# Revit family: VT.VAR11.G.07
name_source: partatom
category: Оборудование
units: mm (PartAtom-declared; Revit-internal decimal feet)

## family parameters
Всегда вертикально = Да
Заголовок OmniClass = Climate Control (HVAC)
На основе рабочей плоскости = Нет
Номер OmniClass = 23.75.00.00
Общий = Нет
При загрузке вырезать с полостями = Нет
Размер круглого соединителя = Использовать диаметр
Тип детали = Нормальный
Точка расчета площади = Нет

## types (1)
- VT.VAR11.G.07
    BIMобъект категории = Другие
    BIMобъект основная категория = Водопровод
    Design country = Italy
    Edition number = 2
    Manifacturer URL = https://valtec.ru
    Manufacturer country = Italy
    Manufacturer name = IVAR
    Nominal height = 0 мм
    Nominal width = 0 мм
    Product SKU = VARIMIX
    Product family = Thermal Power Station
    Product group = Varimix
    Product url = https://valtec.ru
    Revit Version = 2018
    URL = https://valtec.ru
    URL бренда = https://valtec.ru
    Uniclass 1.4 Описание = Климат-контроль установки и оборудование (HVAC)
    Uniclass 2.0 Описание = Клапаны
    Uniclass 2015 = Системы отопления, охлаждения и охлаждения
    Weight Net (Kg) = 0
    Версия EMCS = 3.0
    Группа модели = VAR 11
    Изготовитель = IVAR
    Инструкция по установке = https://valtec.ru
    Классификация IFC = Клапаны
    Код категории BIMобъекта = plumbing-other
    Код основной категории BIMobject = plumbing
    Линия продуктов = ТЕПЛОВАЯ ЭЛЕКТРОСТАНЦИЯ
    Макс рабочая температура (°C) = 120 °C
    Макс рабочее давление (бар) = 10 Па
    Максимальная скорость потока = 3000 l/h
    Мастерформат 2014 Описание = Отопление, вентиляция и кондиционирование воздуха (HVAC)
    Материал = Латунь - CW617N
    Материал основной = Латунь
    Общий поток подачи гидравлики = 0.0 л/с
    Описание = Высокотемпературный комплект прямого потока с байпасом для системы VARIMIX.
    Описание NBS = Valves
    Описание OmniClass = HVAC Specific Products and Equipment
    Описание Конфигурации = Высокотемпературный комплект прямого потока с байпасом для системы VARIMIX.
    Описание статьи = Высокотемпературный комплект прямого потока с байпасом для системы VARIMIX.
    Пенополистрирольная теплоизоляция = Да
    Перепускной клапан перепад давления (бар) = 0.2 - 0.6
    Полный гидравлический возвратный поток = 0.0 л/с
    Практическое руководство по использованию семьи = - Вы можете выбрать версию с или без трехскоростного стандартного насоса. Отметьте эту опцию в параметре «Свойства модели - трехскоростной стандартный насос» или «Свойства модели - нет насоса».
    Произведено в = Made in Italy
    Размер соединения = G 1"1/4 M
    Размеры соединения насоса = G 1"1/2 M
    Техническое описание = https://valtec.ru
    Тип статьи = VAR 11
